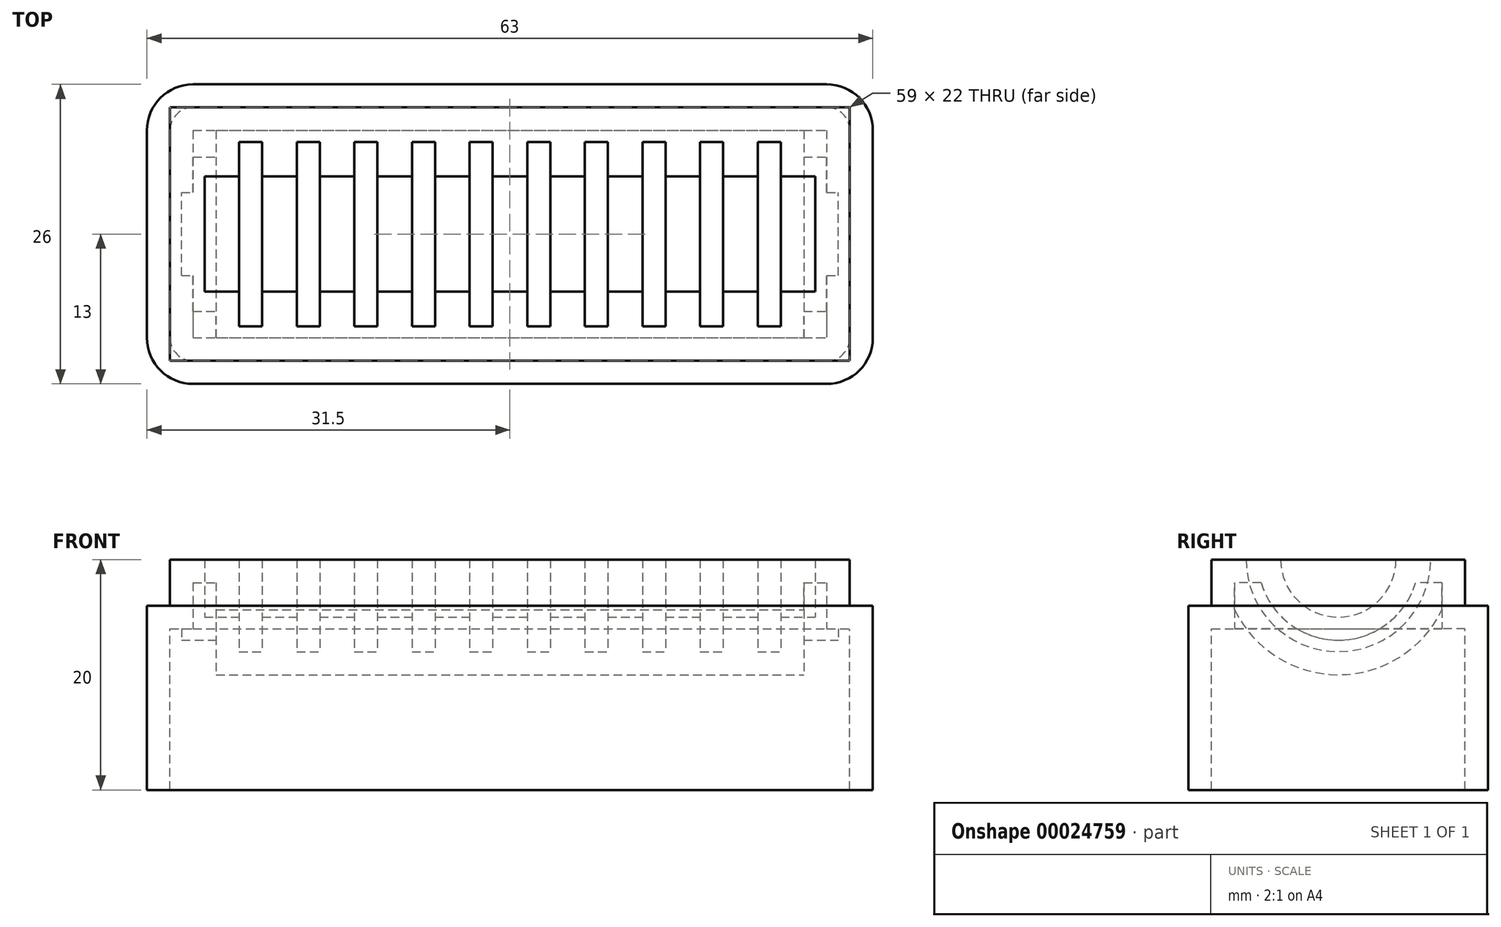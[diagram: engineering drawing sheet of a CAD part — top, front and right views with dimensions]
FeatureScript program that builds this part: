
annotation { "Feature Type Name" : "Feature", "Feature Type Description" : "" }
export const myFeature = defineFeature(function(context is Context, id is Id, definition is map)
    precondition{}
    {
        {
            var Q0;
            Q0=qCreatedBy(makeId("Top.planeOp"),FACE);
            var sketch = newSketch(context, id + "F0", { "sketchPlane" : qUnion([Q0])});
            skLineSegment(sketch, "E0.bottom", {"start": v(4, 0) * mm, "end": v(59, 0) * mm});
            skLineSegment(sketch, "E0.top", {"start": v(4, 26) * mm, "end": v(59, 26) * mm});
            skLineSegment(sketch, "E0.left", {"start": v(0, 4) * mm, "end": v(0, 22) * mm});
            skLineSegment(sketch, "E0.right", {"start": v(63, 4) * mm, "end": v(63, 22) * mm});
            skPoint(sketch, "E1.visualSharp", {"position": v(0, 26) * mm});
            skArc(sketch, "E1.filletArc", {"start": v(4, 26) * mm, "mid": v(1.17, 24.83) * mm, "end": v(0, 22) * mm});
            skPoint(sketch, "E2.visualSharp", {"position": v(63, 26) * mm});
            skArc(sketch, "E2.filletArc", {"start": v(63, 22) * mm, "mid": v(61.83, 24.83) * mm, "end": v(59, 26) * mm});
            skPoint(sketch, "E3.visualSharp", {"position": v(63, 0) * mm});
            skArc(sketch, "E3.filletArc", {"start": v(59, 0) * mm, "mid": v(61.83, 1.17) * mm, "end": v(63, 4) * mm});
            skPoint(sketch, "E4.visualSharp", {"position": v(0, 0) * mm});
            skArc(sketch, "E4.filletArc", {"start": v(0, 4) * mm, "mid": v(1.17, 1.17) * mm, "end": v(4, 0) * mm});
            skSolve(sketch);
        }
        {
            var Q0;
            Q0 = qSketchRegion(id + "F0", true);
            extrude(context, id + "F1", {"entities" : qUnion([Q0]), "depth" : 16 * mm});
        }
        {
            var Q0;
            Q0=makeQuery(id+"F1.opExtrude","CAP_FACE",FACE,{"disambiguationData":[OSD([sQuery(id+"F0.wireOp",EDGE,"E0.bottom"),sQuery(id+"F0.wireOp",EDGE,"E0.top"),sQuery(id+"F0.wireOp",EDGE,"E0.left"),sQuery(id+"F0.wireOp",EDGE,"E0.right"),sQuery(id+"F0.wireOp",EDGE,"E1.filletArc"),sQuery(id+"F0.wireOp",EDGE,"E2.filletArc"),sQuery(id+"F0.wireOp",EDGE,"E3.filletArc"),sQuery(id+"F0.wireOp",EDGE,"E4.filletArc")])],"isStart":false});
            var sketch = newSketch(context, id + "F2", { "sketchPlane" : qUnion([Q0])});
            skLineSegment(sketch, "E5.bottom", {"start": v(2, 24) * mm, "end": v(61, 24) * mm});
            skLineSegment(sketch, "E5.top", {"start": v(2, 2) * mm, "end": v(61, 2) * mm});
            skLineSegment(sketch, "E5.left", {"start": v(2, 24) * mm, "end": v(2, 2) * mm});
            skLineSegment(sketch, "E5.right", {"start": v(61, 24) * mm, "end": v(61, 2) * mm});
            skSolve(sketch);
        }
        {
            var Q0;
            Q0 = qSketchRegion(id + "F2", true);
            extrude(context, id + "F3", {"entities" : qUnion([Q0]), "operationType" : NewBodyOperationType.ADD, "depth" : 4 * mm});
        }
        {
            var Q0;
            Q0=makeQuery(id+"F3.opExtrude","CAP_FACE",FACE,{"disambiguationData":[OSD([sQuery(id+"F2.wireOp",EDGE,"E5.bottom"),sQuery(id+"F2.wireOp",EDGE,"E5.top"),sQuery(id+"F2.wireOp",EDGE,"E5.left"),sQuery(id+"F2.wireOp",EDGE,"E5.right")])],"isStart":false});
            var sketch = newSketch(context, id + "F4", { "sketchPlane" : qUnion([Q0])});
            skLineSegment(sketch, "E6", {"start": v(2, 13) * mm, "end": v(61, 13) * mm, "construction": true});
            skLineSegment(sketch, "E7.bottom", {"start": v(5, 13) * mm, "end": v(58, 13) * mm});
            skLineSegment(sketch, "E7.top", {"start": v(5, 21) * mm, "end": v(58, 21) * mm});
            skLineSegment(sketch, "E7.left", {"start": v(5, 13) * mm, "end": v(5, 21) * mm});
            skLineSegment(sketch, "E7.right", {"start": v(58, 13) * mm, "end": v(58, 21) * mm});
            skLineSegment(sketch, "E8.bottom", {"start": v(5, 21) * mm, "end": v(8, 21) * mm});
            skLineSegment(sketch, "E8.top", {"start": v(5, 18) * mm, "end": v(8, 18) * mm});
            skLineSegment(sketch, "E8.left", {"start": v(5, 21) * mm, "end": v(5, 18) * mm});
            skLineSegment(sketch, "E8.right", {"start": v(8, 21) * mm, "end": v(8, 18) * mm});
            skLineSegment(sketch, "E9.1.0.0", {"start": v(13, 21) * mm, "end": v(13, 18) * mm});
            skLineSegment(sketch, "E9.1.0.1", {"start": v(10, 18) * mm, "end": v(13, 18) * mm});
            skLineSegment(sketch, "E9.1.0.2", {"start": v(10, 21) * mm, "end": v(13, 21) * mm});
            skLineSegment(sketch, "E9.1.0.3", {"start": v(10, 21) * mm, "end": v(10, 18) * mm});
            skLineSegment(sketch, "E9.2.0.0", {"start": v(18, 21) * mm, "end": v(18, 18) * mm});
            skLineSegment(sketch, "E9.2.0.1", {"start": v(15, 18) * mm, "end": v(18, 18) * mm});
            skLineSegment(sketch, "E9.2.0.2", {"start": v(15, 21) * mm, "end": v(18, 21) * mm});
            skLineSegment(sketch, "E9.2.0.3", {"start": v(15, 21) * mm, "end": v(15, 18) * mm});
            skLineSegment(sketch, "E9.3.0.0", {"start": v(23, 21) * mm, "end": v(23, 18) * mm});
            skLineSegment(sketch, "E9.3.0.1", {"start": v(20, 18) * mm, "end": v(23, 18) * mm});
            skLineSegment(sketch, "E9.3.0.2", {"start": v(20, 21) * mm, "end": v(23, 21) * mm});
            skLineSegment(sketch, "E9.3.0.3", {"start": v(20, 21) * mm, "end": v(20, 18) * mm});
            skLineSegment(sketch, "E9.4.0.0", {"start": v(28, 21) * mm, "end": v(28, 18) * mm});
            skLineSegment(sketch, "E9.4.0.1", {"start": v(25, 18) * mm, "end": v(28, 18) * mm});
            skLineSegment(sketch, "E9.4.0.2", {"start": v(25, 21) * mm, "end": v(28, 21) * mm});
            skLineSegment(sketch, "E9.4.0.3", {"start": v(25, 21) * mm, "end": v(25, 18) * mm});
            skLineSegment(sketch, "E9.5.0.0", {"start": v(33, 21) * mm, "end": v(33, 18) * mm});
            skLineSegment(sketch, "E9.5.0.1", {"start": v(30, 18) * mm, "end": v(33, 18) * mm});
            skLineSegment(sketch, "E9.5.0.2", {"start": v(30, 21) * mm, "end": v(33, 21) * mm});
            skLineSegment(sketch, "E9.5.0.3", {"start": v(30, 21) * mm, "end": v(30, 18) * mm});
            skLineSegment(sketch, "E9.6.0.0", {"start": v(38, 21) * mm, "end": v(38, 18) * mm});
            skLineSegment(sketch, "E9.6.0.1", {"start": v(35, 18) * mm, "end": v(38, 18) * mm});
            skLineSegment(sketch, "E9.6.0.2", {"start": v(35, 21) * mm, "end": v(38, 21) * mm});
            skLineSegment(sketch, "E9.6.0.3", {"start": v(35, 21) * mm, "end": v(35, 18) * mm});
            skLineSegment(sketch, "E9.7.0.0", {"start": v(43, 21) * mm, "end": v(43, 18) * mm});
            skLineSegment(sketch, "E9.7.0.1", {"start": v(40, 18) * mm, "end": v(43, 18) * mm});
            skLineSegment(sketch, "E9.7.0.2", {"start": v(40, 21) * mm, "end": v(43, 21) * mm});
            skLineSegment(sketch, "E9.7.0.3", {"start": v(40, 21) * mm, "end": v(40, 18) * mm});
            skLineSegment(sketch, "E9.8.0.0", {"start": v(48, 21) * mm, "end": v(48, 18) * mm});
            skLineSegment(sketch, "E9.8.0.1", {"start": v(45, 18) * mm, "end": v(48, 18) * mm});
            skLineSegment(sketch, "E9.8.0.2", {"start": v(45, 21) * mm, "end": v(48, 21) * mm});
            skLineSegment(sketch, "E9.8.0.3", {"start": v(45, 21) * mm, "end": v(45, 18) * mm});
            skLineSegment(sketch, "E9.9.0.0", {"start": v(53, 21) * mm, "end": v(53, 18) * mm});
            skLineSegment(sketch, "E9.9.0.1", {"start": v(50, 18) * mm, "end": v(53, 18) * mm});
            skLineSegment(sketch, "E9.9.0.2", {"start": v(50, 21) * mm, "end": v(53, 21) * mm});
            skLineSegment(sketch, "E9.9.0.3", {"start": v(50, 21) * mm, "end": v(50, 18) * mm});
            skLineSegment(sketch, "E9.10.0.0", {"start": v(58, 21) * mm, "end": v(58, 18) * mm});
            skLineSegment(sketch, "E9.10.0.1", {"start": v(55, 18) * mm, "end": v(58, 18) * mm});
            skLineSegment(sketch, "E9.10.0.2", {"start": v(55, 21) * mm, "end": v(58, 21) * mm});
            skLineSegment(sketch, "E9.10.0.3", {"start": v(55, 21) * mm, "end": v(55, 18) * mm});
            skLineSegment(sketch, "E9.direction1", {"start": v(8, 18) * mm, "end": v(13, 18) * mm, "construction": true});
            skSolve(sketch);
        }
        {
            var Q0;
            Q0=makeQuery(id+"F4.imprint","IMPRINT",FACE,{"disambiguationData":[TD([[makeQuery(id+"F4.imprint","IMPRINT",EDGE,{"derivedFrom":sQuery(id+"F4.wireOp",EDGE,"E7.bottom")}),1.0]])]});
            var Q1;
            Q1=sQuery(id+"F4.wireOp",EDGE,"E7.bottom");
            revolve(context, id + "F5", {"operationType" : NewBodyOperationType.REMOVE, "entities" : qUnion([Q0]), "axis" : qUnion([Q1]), "revolveType" : RevolveType.ONE_DIRECTION, "oppositeDirection" : true, "angle" : 180 * degree});
        }
        {
            var Q0;
            Q0=makeQuery(id+"F1.opExtrude","CAP_FACE",FACE,{"disambiguationData":[OSD([sQuery(id+"F0.wireOp",EDGE,"E0.bottom"),sQuery(id+"F0.wireOp",EDGE,"E0.top"),sQuery(id+"F0.wireOp",EDGE,"E0.left"),sQuery(id+"F0.wireOp",EDGE,"E0.right"),sQuery(id+"F0.wireOp",EDGE,"E1.filletArc"),sQuery(id+"F0.wireOp",EDGE,"E2.filletArc"),sQuery(id+"F0.wireOp",EDGE,"E3.filletArc"),sQuery(id+"F0.wireOp",EDGE,"E4.filletArc")])],"isStart":true});
            shell(context, id + "F6", {"entities" : qUnion([Q0]), "thickness" : 2 * mm});
        }
    });
